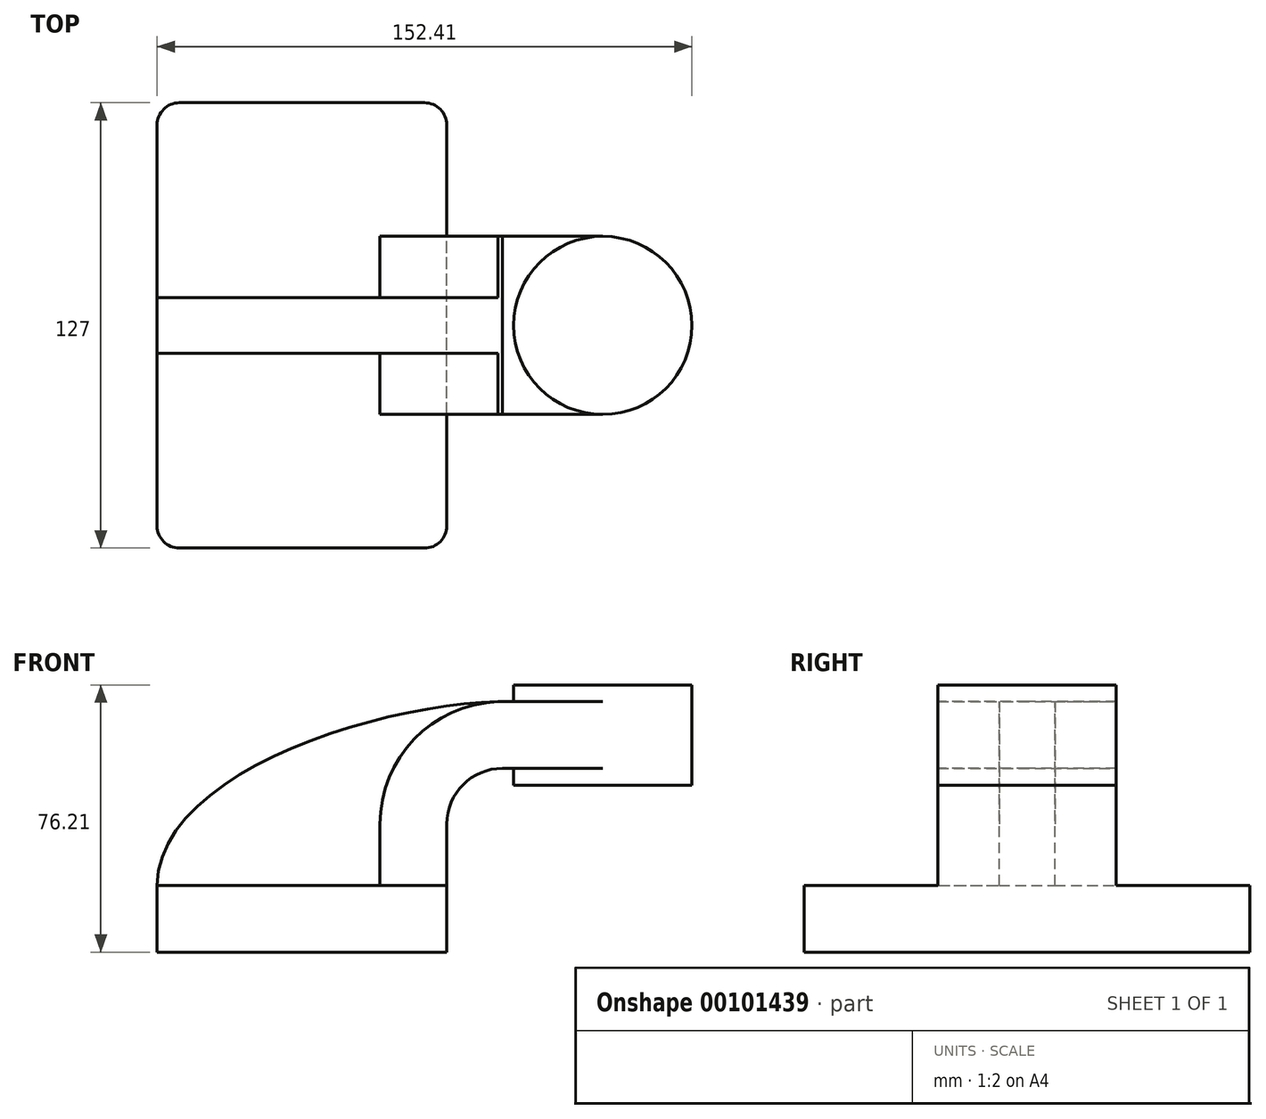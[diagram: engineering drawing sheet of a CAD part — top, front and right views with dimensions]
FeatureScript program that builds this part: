
annotation { "Feature Type Name" : "Feature", "Feature Type Description" : "" }
export const myFeature = defineFeature(function(context is Context, id is Id, definition is map)
    precondition{}
    {
        {
            var Q0;
            Q0=qCreatedBy(makeId("Front.planeOp"),FACE);
            var sketch = newSketch(context, id + "F0", { "sketchPlane" : qUnion([Q0])});
            skLineSegment(sketch, "E0.bottom", {"start": v(-41.28, 9.52) * mm, "end": v(41.28, 9.53) * mm});
            skLineSegment(sketch, "E0.top", {"start": v(-41.28, -9.53) * mm, "end": v(41.28, -9.53) * mm});
            skLineSegment(sketch, "E0.left", {"start": v(-41.28, 9.52) * mm, "end": v(-41.28, -9.53) * mm});
            skLineSegment(sketch, "E0.right", {"start": v(41.28, 9.53) * mm, "end": v(41.28, -9.52) * mm});
            skPoint(sketch, "E0.middle", {"position": v(0, 0) * mm});
            skLineSegment(sketch, "E1.bottom", {"start": v(60.32, 66.67) * mm, "end": v(111.12, 66.67) * mm});
            skLineSegment(sketch, "E1.top", {"start": v(60.32, 38.1) * mm, "end": v(111.12, 38.1) * mm});
            skLineSegment(sketch, "E1.left", {"start": v(60.32, 66.67) * mm, "end": v(60.32, 38.1) * mm});
            skLineSegment(sketch, "E1.right", {"start": v(111.12, 66.67) * mm, "end": v(111.12, 38.1) * mm});
            skPoint(sketch, "E1.middle", {"position": v(85.72, 52.39) * mm});
            skLineSegment(sketch, "E2", {"start": v(41.27, 9.53) * mm, "end": v(41.27, 27) * mm});
            skArc(sketch, "E3", {"start": v(41.27, 27) * mm, "mid": v(45.92, 38.23) * mm, "end": v(57.15, 42.88) * mm});
            skLineSegment(sketch, "E4", {"start": v(57.15, 42.88) * mm, "end": v(85.72, 42.88) * mm});
            skLineSegment(sketch, "E5.0", {"start": v(57.15, 61.93) * mm, "end": v(85.72, 61.93) * mm});
            skArc(sketch, "E5.1", {"start": v(22.22, 27) * mm, "mid": v(32.45, 51.7) * mm, "end": v(57.15, 61.93) * mm});
            skLineSegment(sketch, "E5.2", {"start": v(22.22, 9.53) * mm, "end": v(22.22, 27) * mm});
            skLineSegment(sketch, "E6", {"start": v(85.72, 38.1) * mm, "end": v(85.72, 66.67) * mm});
            skFitSpline(sketch, "E7", {"points": [v(-41.28, 9.53) * mm, v(57.15, 61.93) * mm], "startDerivative": vector(1.34, 97.83) * mm, "endDerivative": vector(102.8, 1.24) * mm});
            skSolve(sketch);
        }
        {
            var Q0;
            Q0=makeQuery(id+"F0.imprint","IMPRINT",FACE,{"disambiguationData":[TD([[makeQuery(id+"F0.imprint","IMPRINT",EDGE,{"derivedFrom":sQuery(id+"F0.wireOp",EDGE,"E0.top")}),1.0]])]});
            extrude(context, id + "F1", {"entities" : qUnion([Q0]), "endBound" : BoundingType.SYMMETRIC, "depth" : 127 * mm});
        }
        {
            var Q0;
            {var subQ1=sQuery(id+"F0.wireOp",EDGE,"E2");Q0=makeQuery(id+"F0.imprint","IMPRINT",FACE,{"disambiguationData":[TD([[makeQuery(id+"F0.imprint","IMPRINT",EDGE,{"derivedFrom":subQ1}),1.0]])]});}
            var Q1;
            {var subQ0=sQuery(id+"F0.wireOp",EDGE,"E5.0");var subQ1=sQuery(id+"F0.wireOp",EDGE,"E1.left");var subQ2=makeQuery(id+"F0.imprint","INTERSECT",VERTEX,{"derivedFrom":[subQ1,subQ0]});Q1=makeQuery(id+"F0.imprint","IMPRINT",FACE,{"disambiguationData":[TD([[makeQuery(id+"F0.imprint","IMPRINT",EDGE,{"disambiguationData":[TD([[subQ2,-1.0]])],"derivedFrom":subQ1}),1.0]])]});}
            extrude(context, id + "F2", {"entities" : qUnion([Q0, Q1]), "operationType" : NewBodyOperationType.ADD, "endBound" : BoundingType.SYMMETRIC, "depth" : 50.8 * mm});
        }
        {
            var Q0;
            {var subQ3=sQuery(id+"F0.wireOp",EDGE,"E5.2");Q0=makeQuery(id+"F0.imprint","IMPRINT",FACE,{"disambiguationData":[TD([[makeQuery(id+"F0.imprint","IMPRINT",EDGE,{"derivedFrom":subQ3}),1.0]])]});}
            extrude(context, id + "F3", {"entities" : qUnion([Q0]), "operationType" : NewBodyOperationType.ADD, "endBound" : BoundingType.SYMMETRIC, "depth" : 15.88 * mm});
        }
        {
            var Q0;
            {var subQ0=sQuery(id+"F0.wireOp",EDGE,"E1.right");Q0=makeQuery(id+"F0.imprint","IMPRINT",FACE,{"disambiguationData":[TD([[makeQuery(id+"F0.imprint","IMPRINT",EDGE,{"derivedFrom":subQ0}),-1.0]])]});}
            var Q1;
            Q1=sQuery(id+"F0.wireOp",EDGE,"E6");
            revolve(context, id + "F4", {"operationType" : NewBodyOperationType.ADD, "entities" : qUnion([Q0]), "axis" : qUnion([Q1]), "revolveType" : RevolveType.FULL});
        }
        {
            var Q0;
            Q0=makeQuery(id+"F1.opExtrude","CAP_EDGE",EDGE,{"disambiguationData":[OSD([sQuery(id+"F0.wireOp",EDGE,"E0.right")])],"isStart":true});
            var Q1;
            Q1=makeQuery(id+"F1.opExtrude","CAP_EDGE",EDGE,{"disambiguationData":[OSD([sQuery(id+"F0.wireOp",EDGE,"E0.left")])],"isStart":true});
            var Q2;
            Q2=makeQuery(id+"F1.opExtrude","CAP_EDGE",EDGE,{"disambiguationData":[OSD([sQuery(id+"F0.wireOp",EDGE,"E0.left")])],"isStart":false});
            var Q3;
            Q3=makeQuery(id+"F1.opExtrude","CAP_EDGE",EDGE,{"disambiguationData":[OSD([sQuery(id+"F0.wireOp",EDGE,"E0.right")])],"isStart":false});
            fillet(context, id + "F5", {"entities" : qUnion([Q0, Q1, Q2, Q3]), "radius" : 6.35 * mm, "tangentPropagation" : true, "allowEdgeOverflow" : false});
        }
    });
